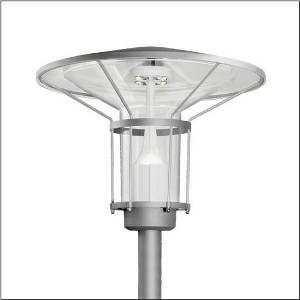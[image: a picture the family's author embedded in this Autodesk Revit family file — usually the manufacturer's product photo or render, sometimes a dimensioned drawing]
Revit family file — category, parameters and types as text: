
# Revit family: laterne_classic_iq___p1_0a_5xa5245ff14h000022_892e
name_source: partatom
category: Lighting Fixtures
units: mm (PartAtom-declared; Revit-internal decimal feet)

## family parameters
Cut with Voids When Loaded = No
Host = Face
Light Source = No
Part Type = Normal
Room Calculation Point = No
Round Connector Dimension = Use Diameter
Shared = No

## types (1)
- --- (1 x LED, 1360 lm, 10.5 W, 3000K)
    Apparent Load = 11 VA
    CIE Flux Codes = 30 61 91 96 100
    Color Rendering = 70
    Color Temperature = 3000K
    Default Elevation = 1800 mm
    Description = Lantern Classic iQ, mast luminaire, Module 540 iQ-SR, primary light control with 3 zone facetted reflector, of plastic, silver coated, highly specular, structured, primary optical cover: cover, of PMMA, transparent, light distribution: P1.0a, light emission: direct distribution, primary light characteristic: strongly asymmetric, installation type: post-top, LED, High Power LED, rated luminous flux: 1.360lm, luminous efficacy: 130lm/W, light colour: 730, colour temperature: 3000K, control gear: iQ Street-Remote, control: Street-Remote, Auto-Match, Temp-Guard, Lumen-Switch, Night-Set, Smart-Wire, Light-Fading, Desk-Remote (wireless, voltage-free reading and setting of iQ features in the workshop via application-optimized NFC function/RFID function), optimised constant luminous flux control (CLO 2.0), pre-setting: logarithmic dimming characteristic, mains connection: 230..240V, AC, 50/60Hz, connection cable pre-assembled, cable length: 5,5m, wiring characteristics: H07RN-F, start of lifetime: 11W, end of service life: 11W, reduction: 5W, luminaire housing, upper part, of glass-fibre reinforced polyester, coated, Siteco® metallic grey (DB 702S), diameter: 750mm, height: 596mm, spigot size: d x l = 76 x 70mm (post-top) | with reducer (optional accessory) 60 x 70mm, mounting height: 3..5m, post-top mast mounting element, of diecast aluminium, coated, Siteco® metallic grey (DB 702S), Module 540 iQ-SR, traffic white (RAL 9016), equipment: standard, protection rating (complete): IP65, insulation class (complete): insulation class II (safety insulation), certification: CE, ENEC, VDE, packaging unit: 1 piece

Light Distribution: P1.0a
    Height = 596 mm
    Lamp = 1 x LED
    Lamp Light Flux = 1360 lm
    Lamp Power = 10.5 W
    Lamp count = 1
    Length = 750 mm
    Luminous efficacy = 130 lm/W
    Manufacturer = Siteco
    ModVariant = No
    Model = 5XA5245FF14H000022
    Number of Poles = 1
    OnlyDefault = Yes
    Power Factor = 1
    Product Name = Laterne Classic iQ | P1.0a
    Product group = mast luminaire | pylon top
    ProductGroupID = 6100
    Protection Class = Protection class II
    Protection Degree = IP 65
    RLX_Detail_Level = 1
    RLX_Emergency_Light_Flux = 0 lm
    RLX_Emergency_Type = 0
    RLX_Emergency_Type_DB = No
    RlxData = <blob elided: 39769 chars, md5=8dc51faf>
    Socket = socket
    Standby Power = 0 W
    System Light Flux = 1360 lm
    System Power = 11 W
    Type Comments = factory setting: luminous flux: 100 % | dim-lin: 254 | 419 mA
    Type Image = l_1006052.jpg
    URL = http://relux.com
    VarID = @adj_160206
    Voltage = 0 V
    Weight = 0.00 kg
    Width = 0 mm  [stored 0 ft]

note: [stored X ft] marks values corroborated as IEEE doubles in the binary element streams (Revit-internal decimal feet)

## geometry (parser evidence)
native form markers: Blend x4, Sweep x9
no freeform markers — native parametric forms only
